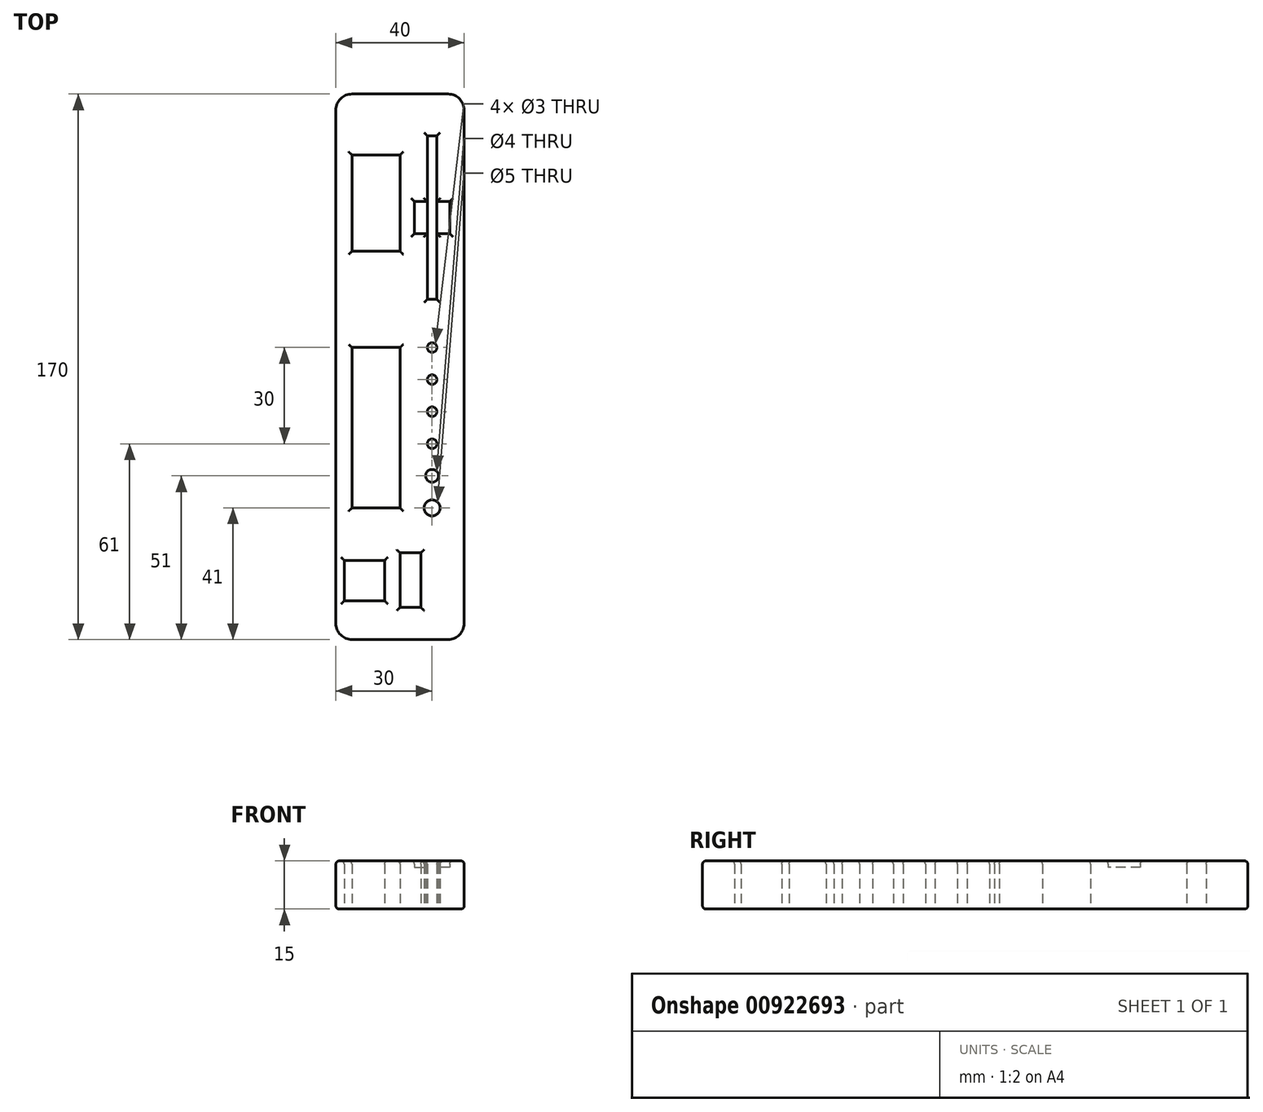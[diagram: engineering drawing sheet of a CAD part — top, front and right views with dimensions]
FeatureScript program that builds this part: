
annotation { "Feature Type Name" : "Feature", "Feature Type Description" : "" }
export const myFeature = defineFeature(function(context is Context, id is Id, definition is map)
    precondition{}
    {
        {
            var Q0;
            Q0=qCreatedBy(makeId("Top.planeOp"),FACE);
            var sketch = newSketch(context, id + "F0", { "sketchPlane" : qUnion([Q0])});
            skLineSegment(sketch, "E0", {"start": v(0, 0) * mm, "end": v(40, 0) * mm});
            skLineSegment(sketch, "E1", {"start": v(40, 0) * mm, "end": v(40, 170) * mm});
            skLineSegment(sketch, "E2", {"start": v(40, 170) * mm, "end": v(0, 170) * mm});
            skLineSegment(sketch, "E3", {"start": v(0, 170) * mm, "end": v(0, 0) * mm});
            skLineSegment(sketch, "E4", {"start": v(20, 0) * mm, "end": v(20, 170) * mm});
            skLineSegment(sketch, "E5", {"start": v(20, 0) * mm, "end": v(20, 10) * mm});
            skLineSegment(sketch, "E6", {"start": v(20, 10) * mm, "end": v(26.5, 10) * mm});
            skLineSegment(sketch, "E7", {"start": v(26.5, 10) * mm, "end": v(26.5, 27) * mm});
            skLineSegment(sketch, "E8", {"start": v(26.5, 27) * mm, "end": v(20, 27) * mm});
            skLineSegment(sketch, "E9", {"start": v(20, 27) * mm, "end": v(20, 10) * mm});
            skLineSegment(sketch, "E10", {"start": v(20, 27) * mm, "end": v(20, 41) * mm});
            skLineSegment(sketch, "E11", {"start": v(20, 41) * mm, "end": v(5, 41) * mm});
            skLineSegment(sketch, "E12", {"start": v(5, 41) * mm, "end": v(5, 91) * mm});
            skLineSegment(sketch, "E13", {"start": v(5, 91) * mm, "end": v(20, 91) * mm});
            skLineSegment(sketch, "E14", {"start": v(20, 91) * mm, "end": v(20, 41) * mm});
            skLineSegment(sketch, "E15", {"start": v(20, 91) * mm, "end": v(20, 121) * mm});
            skLineSegment(sketch, "E16", {"start": v(20, 121) * mm, "end": v(5, 121) * mm});
            skLineSegment(sketch, "E17", {"start": v(5, 121) * mm, "end": v(5, 151) * mm});
            skLineSegment(sketch, "E18", {"start": v(5, 151) * mm, "end": v(20, 151) * mm});
            skLineSegment(sketch, "E19", {"start": v(20, 151) * mm, "end": v(20, 121) * mm});
            skLineSegment(sketch, "E20", {"start": v(20, 41) * mm, "end": v(30, 41) * mm});
            skLineSegment(sketch, "E21", {"start": v(30, 41) * mm, "end": v(30, 51) * mm});
            skLineSegment(sketch, "E22", {"start": v(30, 51) * mm, "end": v(30, 61) * mm});
            skLineSegment(sketch, "E23", {"start": v(30, 61) * mm, "end": v(30, 71) * mm});
            skLineSegment(sketch, "E24", {"start": v(30, 71) * mm, "end": v(30, 81) * mm});
            skLineSegment(sketch, "E25", {"start": v(30, 81) * mm, "end": v(30, 91) * mm});
            skCircle(sketch, "E26", {"center": v(30, 41) * mm, "radius": 2.5 * mm});
            skCircle(sketch, "E27", {"center": v(30, 51) * mm, "radius": 2 * mm});
            skCircle(sketch, "E28", {"center": v(30, 61) * mm, "radius": 1.5 * mm});
            skCircle(sketch, "E29", {"center": v(30, 71) * mm, "radius": 1.5 * mm});
            skCircle(sketch, "E30", {"center": v(30, 81) * mm, "radius": 1.5 * mm});
            skCircle(sketch, "E31", {"center": v(30, 91) * mm, "radius": 1.5 * mm});
            skLineSegment(sketch, "E32", {"start": v(30, 91) * mm, "end": v(30, 106) * mm});
            skLineSegment(sketch, "E33", {"start": v(30, 106) * mm, "end": v(30, 157) * mm});
            skLineSegment(sketch, "E34", {"start": v(30, 157) * mm, "end": v(31.5, 157) * mm});
            skLineSegment(sketch, "E35", {"start": v(31.5, 157) * mm, "end": v(31.5, 106) * mm});
            skLineSegment(sketch, "E36", {"start": v(31.5, 106) * mm, "end": v(28.5, 106) * mm});
            skLineSegment(sketch, "E37", {"start": v(28.5, 106) * mm, "end": v(28.5, 157) * mm});
            skLineSegment(sketch, "E38", {"start": v(28.5, 157) * mm, "end": v(30, 157) * mm});
            skLineSegment(sketch, "E39", {"start": v(28.5, 106) * mm, "end": v(28.5, 131.5) * mm});
            skLineSegment(sketch, "E40.bottom", {"start": v(2.58, 24.68) * mm, "end": v(15.23, 24.68) * mm});
            skLineSegment(sketch, "E40.top", {"start": v(2.58, 12.03) * mm, "end": v(15.23, 12.03) * mm});
            skLineSegment(sketch, "E40.left", {"start": v(2.58, 24.68) * mm, "end": v(2.58, 12.03) * mm});
            skLineSegment(sketch, "E40.right", {"start": v(15.23, 24.68) * mm, "end": v(15.23, 12.03) * mm});
            skPoint(sketch, "E40.middle", {"position": v(8.9, 18.35) * mm});
            skLineSegment(sketch, "E41", {"start": v(24.5, 126.5) * mm, "end": v(28.5, 126.5) * mm});
            skLineSegment(sketch, "E42", {"start": v(24.5, 136.5) * mm, "end": v(28.5, 136.5) * mm});
            skLineSegment(sketch, "E43.MirrorCS", {"start": v(35.5, 136.5) * mm, "end": v(31.5, 136.5) * mm});
            skLineSegment(sketch, "E44", {"start": v(24.5, 136.5) * mm, "end": v(24.5, 126.5) * mm});
            skLineSegment(sketch, "E45.MirrorCS", {"start": v(35.5, 136.5) * mm, "end": v(35.5, 126.5) * mm});
            skLineSegment(sketch, "E46.MirrorCS", {"start": v(35.5, 126.5) * mm, "end": v(31.5, 126.5) * mm});
            skSolve(sketch);
        }
        {
            var Q0;
            {var subQ1=sQuery(id+"F0.wireOp",EDGE,"E3");Q0=makeQuery(id+"F0.imprint","IMPRINT",FACE,{"disambiguationData":[TD([[makeQuery(id+"F0.imprint","IMPRINT",EDGE,{"derivedFrom":subQ1}),1.0]])]});}
            var Q1;
            {var subQ21=sQuery(id+"F0.wireOp",EDGE,"E1");Q1=makeQuery(id+"F0.imprint","IMPRINT",FACE,{"disambiguationData":[TD([[makeQuery(id+"F0.imprint","IMPRINT",EDGE,{"derivedFrom":subQ21}),1.0]])]});}
            var Q2;
            {var subQ4=sQuery(id+"F0.wireOp",EDGE,"z8Mk48YQ-2CJq-LB0O-4J4J-8mnZBSXu9I69");Q2=makeQuery(id+"F0.imprint","IMPRINT",FACE,{"disambiguationData":[TD([[makeQuery(id+"F0.imprint","IMPRINT",EDGE,{"derivedFrom":subQ4}),-1.0]])]});}
            var Q3;
            {var subQ0=sQuery(id+"F0.wireOp",EDGE,"5442cd6a-636f-4c31-b873-d7978edb90df0.MirrorCS");Q3=makeQuery(id+"F0.imprint","IMPRINT",FACE,{"disambiguationData":[TD([[makeQuery(id+"F0.imprint","IMPRINT",EDGE,{"derivedFrom":subQ0}),1.0]])]});}
            extrude(context, id + "F1", {"entities" : qUnion([Q0, Q1, Q2, Q3]), "depth" : 15 * mm, "offsetDistance" : 25 * mm});
        }
        {
            var Q0;
            Q0=makeQuery(id+"F1.opExtrude","CAP_FACE",FACE,{"disambiguationData":[OSD([sQuery(id+"F0.wireOp",EDGE,"E0"),sQuery(id+"F0.wireOp",EDGE,"E1"),sQuery(id+"F0.wireOp",EDGE,"E2"),sQuery(id+"F0.wireOp",EDGE,"E3"),sQuery(id+"F0.wireOp",EDGE,"E6"),sQuery(id+"F0.wireOp",EDGE,"E7"),sQuery(id+"F0.wireOp",EDGE,"E8"),sQuery(id+"F0.wireOp",EDGE,"E9"),sQuery(id+"F0.wireOp",EDGE,"E11"),sQuery(id+"F0.wireOp",EDGE,"E12"),sQuery(id+"F0.wireOp",EDGE,"E13"),sQuery(id+"F0.wireOp",EDGE,"E14"),sQuery(id+"F0.wireOp",EDGE,"E16"),sQuery(id+"F0.wireOp",EDGE,"E17"),sQuery(id+"F0.wireOp",EDGE,"E18"),sQuery(id+"F0.wireOp",EDGE,"E19"),sQuery(id+"F0.wireOp",EDGE,"E26"),sQuery(id+"F0.wireOp",EDGE,"E27"),sQuery(id+"F0.wireOp",EDGE,"E28"),sQuery(id+"F0.wireOp",EDGE,"E29"),sQuery(id+"F0.wireOp",EDGE,"E30"),sQuery(id+"F0.wireOp",EDGE,"E31"),sQuery(id+"F0.wireOp",EDGE,"E34"),sQuery(id+"F0.wireOp",EDGE,"E35"),sQuery(id+"F0.wireOp",EDGE,"E36"),sQuery(id+"F0.wireOp",EDGE,"E37"),sQuery(id+"F0.wireOp",EDGE,"E38"),sQuery(id+"F0.wireOp",EDGE,"E39")])],"isStart":false});
            fillet(context, id + "F2", {"entities" : qUnion([Q0]), "radius" : 1 * mm, "tangentPropagation" : true, "allowEdgeOverflow" : false});
        }
        {
            var Q0;
            {var subQ0=sQuery(id+"F0.wireOp",EDGE,"E43.MirrorCS");Q0=makeQuery(id+"F0.imprint","IMPRINT",FACE,{"disambiguationData":[TD([[makeQuery(id+"F0.imprint","IMPRINT",EDGE,{"derivedFrom":subQ0}),1.0]])]});}
            var Q1;
            {var subQ0=sQuery(id+"F0.wireOp",EDGE,"E41");Q1=makeQuery(id+"F0.imprint","IMPRINT",FACE,{"disambiguationData":[TD([[makeQuery(id+"F0.imprint","IMPRINT",EDGE,{"derivedFrom":subQ0}),1.0]])]});}
            extrude(context, id + "F3", {"entities" : qUnion([Q0, Q1]), "operationType" : NewBodyOperationType.ADD, "depth" : 13 * mm, "offsetDistance" : 25 * mm});
        }
        {
            var Q0;
            Q0=makeQuery(id+"F1.opExtrude","CAP_EDGE",EDGE,{"disambiguationData":[OSD([sQuery(id+"F0.wireOp",EDGE,"E1")])],"isStart":true});
            var Q1;
            Q1=makeQuery(id+"F1.opExtrude","CAP_EDGE",EDGE,{"disambiguationData":[OSD([sQuery(id+"F0.wireOp",EDGE,"E2")])],"isStart":true});
            var Q2;
            Q2=makeQuery(id+"F1.opExtrude","CAP_EDGE",EDGE,{"disambiguationData":[OSD([sQuery(id+"F0.wireOp",EDGE,"E3")])],"isStart":true});
            var Q3;
            Q3=makeQuery(id+"F1.opExtrude","CAP_EDGE",EDGE,{"disambiguationData":[OSD([sQuery(id+"F0.wireOp",EDGE,"E0")])],"isStart":true});
            fillet(context, id + "F4", {"entities" : qUnion([Q0, Q1, Q2, Q3]), "radius" : 1 * mm, "tangentPropagation" : true, "allowEdgeOverflow" : false});
        }
        {
            var Q0;
            Q0=makeQuery(id+"F1.opExtrude","SWEPT_EDGE",EDGE,{"disambiguationData":[OSD([sQuery(id+"F0.wireOp",EDGE,"E0"),sQuery(id+"F0.wireOp",EDGE,"E1")])]});
            var Q1;
            Q1=makeQuery(id+"F1.opExtrude","SWEPT_EDGE",EDGE,{"disambiguationData":[OSD([sQuery(id+"F0.wireOp",EDGE,"E0"),sQuery(id+"F0.wireOp",EDGE,"E3")])]});
            var Q2;
            Q2=makeQuery(id+"F1.opExtrude","SWEPT_EDGE",EDGE,{"disambiguationData":[OSD([sQuery(id+"F0.wireOp",EDGE,"E2"),sQuery(id+"F0.wireOp",EDGE,"E3")])]});
            var Q3;
            Q3=makeQuery(id+"F1.opExtrude","SWEPT_EDGE",EDGE,{"disambiguationData":[OSD([sQuery(id+"F0.wireOp",EDGE,"E1"),sQuery(id+"F0.wireOp",EDGE,"E2")])]});
            fillet(context, id + "F5", {"entities" : qUnion([Q0, Q1, Q2, Q3]), "radius" : 5 * mm, "tangentPropagation" : true, "allowEdgeOverflow" : false});
        }
    });
